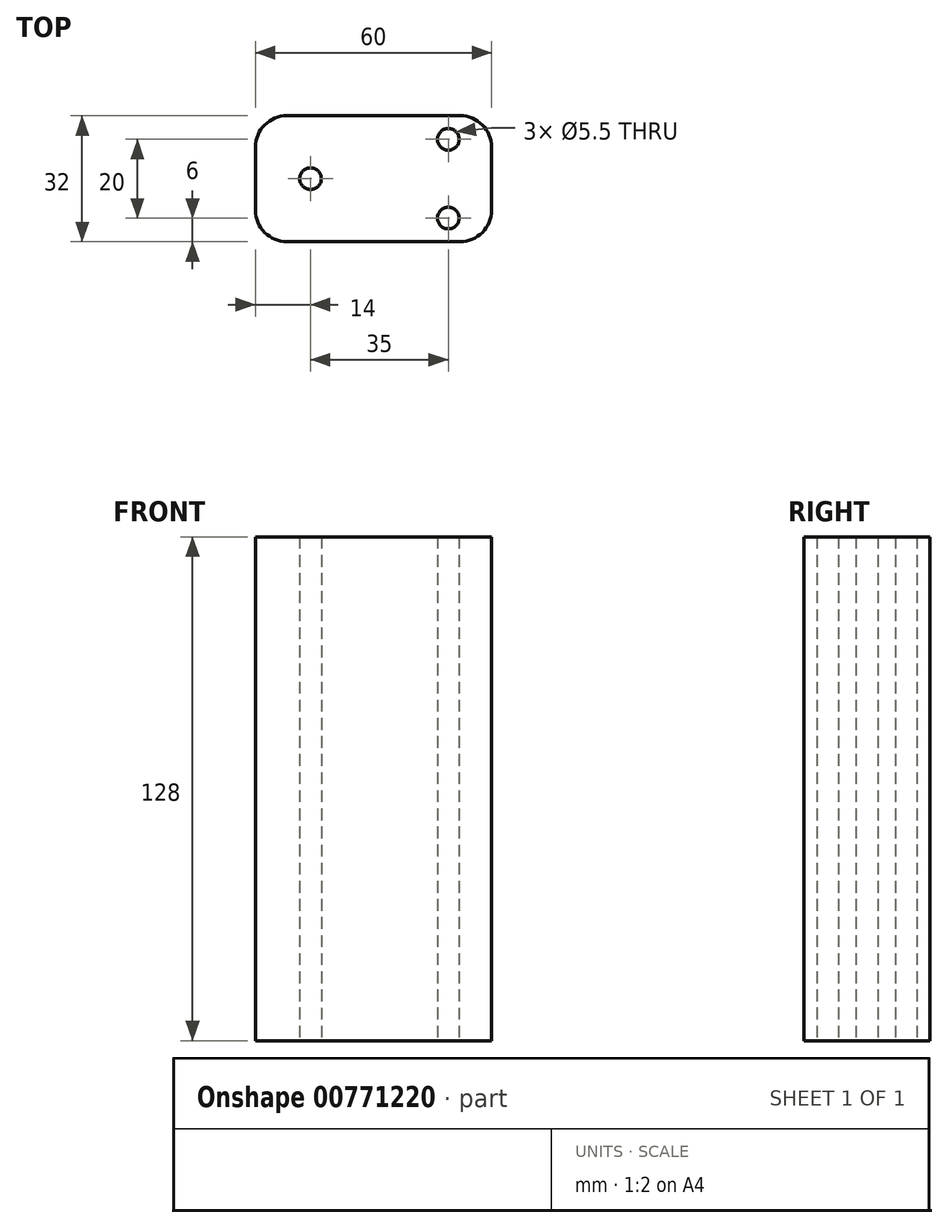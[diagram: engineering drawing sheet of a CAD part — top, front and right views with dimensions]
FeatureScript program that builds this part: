
annotation { "Feature Type Name" : "Feature", "Feature Type Description" : "" }
export const myFeature = defineFeature(function(context is Context, id is Id, definition is map)
    precondition{}
    {
        {
            var Q0;
            Q0=qCreatedBy(makeId("Top.planeOp"),FACE);
            var sketch = newSketch(context, id + "F0", { "sketchPlane" : qUnion([Q0])});
            skLineSegment(sketch, "E0.bottom", {"start": v(52, 32) * mm, "end": v(8, 32) * mm});
            skLineSegment(sketch, "E0.top", {"start": v(52, 0) * mm, "end": v(8, 0) * mm});
            skLineSegment(sketch, "E0.left", {"start": v(60, 24) * mm, "end": v(60, 8) * mm});
            skLineSegment(sketch, "E0.right", {"start": v(0, 24) * mm, "end": v(0, 8) * mm});
            skCircle(sketch, "E1", {"center": v(14, 16) * mm, "radius": 2.75 * mm});
            skCircle(sketch, "E2", {"center": v(49, 6) * mm, "radius": 2.75 * mm});
            skCircle(sketch, "E3", {"center": v(49, 26) * mm, "radius": 2.75 * mm});
            skPoint(sketch, "E4.visualSharp", {"position": v(60, 32) * mm});
            skArc(sketch, "E4.filletArc", {"start": v(60, 24) * mm, "mid": v(57.66, 29.66) * mm, "end": v(52, 32) * mm});
            skPoint(sketch, "E5.visualSharp", {"position": v(0, 32) * mm});
            skArc(sketch, "E5.filletArc", {"start": v(8, 32) * mm, "mid": v(2.34, 29.66) * mm, "end": v(0, 24) * mm});
            skPoint(sketch, "E6.visualSharp", {"position": v(0, 0) * mm});
            skArc(sketch, "E6.filletArc", {"start": v(0, 8) * mm, "mid": v(2.34, 2.34) * mm, "end": v(8, 0) * mm});
            skPoint(sketch, "E7.visualSharp", {"position": v(60, 0) * mm});
            skArc(sketch, "E7.filletArc", {"start": v(52, 0) * mm, "mid": v(57.66, 2.34) * mm, "end": v(60, 8) * mm});
            skLineSegment(sketch, "E8", {"start": v(0, 16) * mm, "end": v(49.42, 16) * mm, "construction": true});
            skLineSegment(sketch, "E9", {"start": v(49, 30) * mm, "end": v(49, 2.26) * mm, "construction": true});
            skSolve(sketch);
        }
        {
            var Q0;
            Q0 = qSketchRegion(id + "F0", true);
            extrude(context, id + "F1", {"entities" : qUnion([Q0]), "depth" : 128 * mm, "offsetDistance" : 25 * mm});
        }
    });
